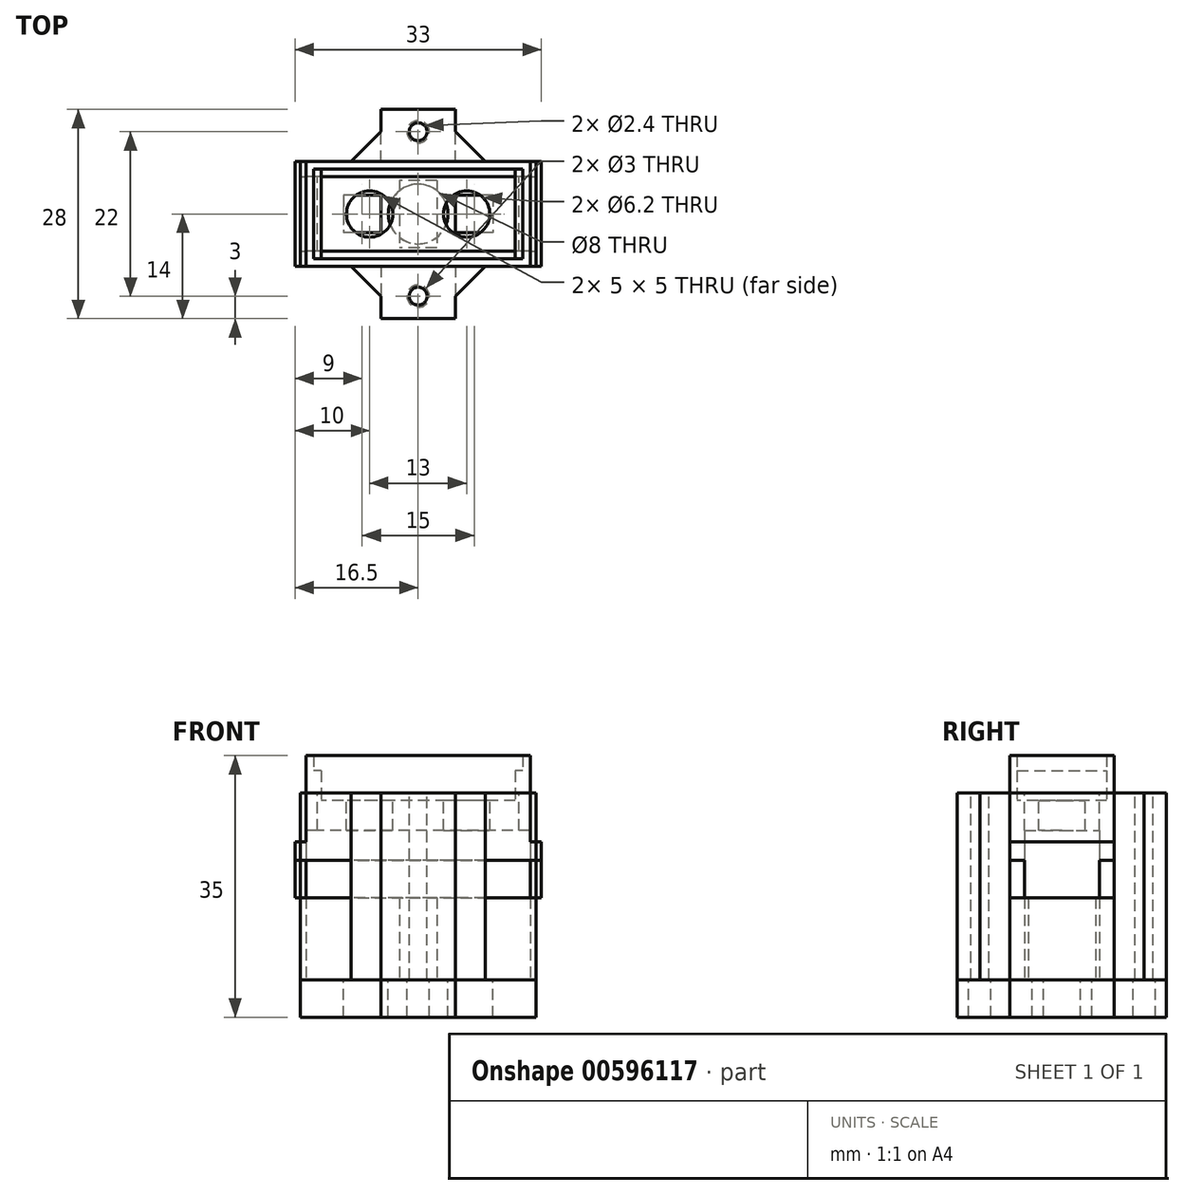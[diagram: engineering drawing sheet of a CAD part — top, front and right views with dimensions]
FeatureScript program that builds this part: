
annotation { "Feature Type Name" : "Feature", "Feature Type Description" : "" }
export const myFeature = defineFeature(function(context is Context, id is Id, definition is map)
    precondition{}
    {
        {
            var Q0;
            Q0=qCreatedBy(makeId("Top.planeOp"),FACE);
            var sketch = newSketch(context, id + "F0", { "sketchPlane" : qUnion([Q0])});
            skLineSegment(sketch, "E0.bottom", {"start": v(15, -7) * mm, "end": v(-15, -7) * mm});
            skLineSegment(sketch, "E0.top", {"start": v(15, 7) * mm, "end": v(-15, 7) * mm});
            skLineSegment(sketch, "E0.left", {"start": v(15, -7) * mm, "end": v(15, 7) * mm});
            skLineSegment(sketch, "E0.right", {"start": v(-15, -7) * mm, "end": v(-15, 7) * mm});
            skPoint(sketch, "E0.middle", {"position": v(0, 0) * mm});
            skSolve(sketch);
        }
        {
            var Q0;
            Q0=qSketchRegion(id+"F0",true);
            extrude(context, id + "F1", {"entities" : qUnion([Q0]), "depth" : 13 * mm, "offsetDistance" : 25 * mm});
        }
        {
            var Q0;
            Q0=makeQuery(id+"F1.opExtrude","CAP_FACE",FACE,{"disambiguationData":[OSD([sQuery(id+"F0.wireOp",EDGE,"E0.bottom"),sQuery(id+"F0.wireOp",EDGE,"E0.top"),sQuery(id+"F0.wireOp",EDGE,"E0.left"),sQuery(id+"F0.wireOp",EDGE,"E0.right")])],"isStart":false});
            var sketch = newSketch(context, id + "F2", { "sketchPlane" : qUnion([Q0])});
            skLineSegment(sketch, "E1.bottom", {"start": v(15, -7) * mm, "end": v(-15, -7) * mm});
            skLineSegment(sketch, "E1.top", {"start": v(15, 7) * mm, "end": v(-15, 7) * mm});
            skLineSegment(sketch, "E1.left", {"start": v(15, -7) * mm, "end": v(15, 7) * mm});
            skLineSegment(sketch, "E1.right", {"start": v(-15, -7) * mm, "end": v(-15, 7) * mm});
            skPoint(sketch, "E1.middle", {"position": v(0, 0) * mm});
            skLineSegment(sketch, "E2.bottom", {"start": v(14, -6) * mm, "end": v(-14, -6) * mm});
            skLineSegment(sketch, "E2.top", {"start": v(14, 6) * mm, "end": v(-14, 6) * mm});
            skLineSegment(sketch, "E2.left", {"start": v(14, -6) * mm, "end": v(14, 6) * mm});
            skLineSegment(sketch, "E2.right", {"start": v(-14, -6) * mm, "end": v(-14, 6) * mm});
            skSolve(sketch);
        }
        {
            var Q0;
            Q0=qSketchRegion(id+"F2",true);
            extrude(context, id + "F3", {"entities" : qUnion([Q0]), "operationType" : NewBodyOperationType.ADD, "depth" : 6 * mm, "offsetDistance" : 25 * mm});
        }
        {
            var Q0;
            Q0=makeQuery(id+"F1.opExtrude","CAP_FACE",FACE,{"disambiguationData":[OSD([sQuery(id+"F0.wireOp",EDGE,"E0.bottom"),sQuery(id+"F0.wireOp",EDGE,"E0.top"),sQuery(id+"F0.wireOp",EDGE,"E0.left"),sQuery(id+"F0.wireOp",EDGE,"E0.right")])],"isStart":false});
            var sketch = newSketch(context, id + "F4", { "sketchPlane" : qUnion([Q0])});
            skLineSegment(sketch, "E3.bottom", {"start": v(-14, 6) * mm, "end": v(-13, 6) * mm});
            skLineSegment(sketch, "E3.top", {"start": v(-14, -6) * mm, "end": v(-13, -6) * mm});
            skLineSegment(sketch, "E3.left", {"start": v(-14, 6) * mm, "end": v(-14, -6) * mm});
            skLineSegment(sketch, "E3.right", {"start": v(-13, 6) * mm, "end": v(-13, -6) * mm});
            skLineSegment(sketch, "E4.bottom", {"start": v(14, 6) * mm, "end": v(13, 6) * mm});
            skLineSegment(sketch, "E4.top", {"start": v(14, -6) * mm, "end": v(13, -6) * mm});
            skLineSegment(sketch, "E4.left", {"start": v(14, 6) * mm, "end": v(14, -6) * mm});
            skLineSegment(sketch, "E4.right", {"start": v(13, 6) * mm, "end": v(13, -6) * mm});
            skSolve(sketch);
        }
        {
            var Q0;
            Q0=qSketchRegion(id+"F4",true);
            extrude(context, id + "F5", {"entities" : qUnion([Q0]), "operationType" : NewBodyOperationType.ADD, "depth" : 4 * mm, "offsetDistance" : 25 * mm});
        }
        {
            var Q0;
            Q0=makeQuery(id+"F1.opExtrude","CAP_FACE",FACE,{"disambiguationData":[OSD([sQuery(id+"F0.wireOp",EDGE,"E0.bottom"),sQuery(id+"F0.wireOp",EDGE,"E0.top"),sQuery(id+"F0.wireOp",EDGE,"E0.left"),sQuery(id+"F0.wireOp",EDGE,"E0.right")])],"isStart":false});
            var sketch = newSketch(context, id + "F6", { "sketchPlane" : qUnion([Q0])});
            skCircle(sketch, "E5", {"center": v(-6.5, 0) * mm, "radius": 3.1 * mm});
            skCircle(sketch, "E6", {"center": v(6.5, 0) * mm, "radius": 3.1 * mm});
            skSolve(sketch);
        }
        {
            var Q0;
            Q0=qSketchRegion(id+"F6",true);
            extrude(context, id + "F7", {"entities" : qUnion([Q0]), "operationType" : NewBodyOperationType.REMOVE, "oppositeDirection" : true, "depth" : 19 * mm, "offsetDistance" : 25 * mm});
        }
        {
            var Q0;
            Q0=makeQuery(id+"F1.opExtrude","CAP_FACE",FACE,{"disambiguationData":[OSD([sQuery(id+"F0.wireOp",EDGE,"E0.bottom"),sQuery(id+"F0.wireOp",EDGE,"E0.top"),sQuery(id+"F0.wireOp",EDGE,"E0.left"),sQuery(id+"F0.wireOp",EDGE,"E0.right")])],"isStart":true});
            var sketch = newSketch(context, id + "F8", { "sketchPlane" : qUnion([Q0])});
            skLineSegment(sketch, "E7.bottom", {"start": v(-15, -7) * mm, "end": v(-16.5, -7) * mm});
            skLineSegment(sketch, "E7.top", {"start": v(-15, 7) * mm, "end": v(-16.5, 7) * mm});
            skLineSegment(sketch, "E7.left", {"start": v(-15, -7) * mm, "end": v(-15, 7) * mm});
            skLineSegment(sketch, "E7.right", {"start": v(-16.5, -7) * mm, "end": v(-16.5, 7) * mm});
            skLineSegment(sketch, "E8.bottom", {"start": v(15, -7) * mm, "end": v(16.5, -7) * mm});
            skLineSegment(sketch, "E8.top", {"start": v(15, 7) * mm, "end": v(16.5, 7) * mm});
            skLineSegment(sketch, "E8.left", {"start": v(15, -7) * mm, "end": v(15, 7) * mm});
            skLineSegment(sketch, "E8.right", {"start": v(16.5, -7) * mm, "end": v(16.5, 7) * mm});
            skSolve(sketch);
        }
        {
            var Q0;
            Q0=qSketchRegion(id+"F8",true);
            extrude(context, id + "F9", {"entities" : qUnion([Q0]), "operationType" : NewBodyOperationType.ADD, "oppositeDirection" : true, "depth" : 7.5 * mm, "offsetDistance" : 25 * mm});
        }
        {
            var Q0;
            Q0=makeQuery(id+"F9.boolean.opBoolean","MERGE",FACE,{"derivedFrom":[makeQuery(id+"F1.opExtrude","CAP_FACE",FACE,{"disambiguationData":[OSD([sQuery(id+"F0.wireOp",EDGE,"E0.bottom"),sQuery(id+"F0.wireOp",EDGE,"E0.top"),sQuery(id+"F0.wireOp",EDGE,"E0.left"),sQuery(id+"F0.wireOp",EDGE,"E0.right")])],"isStart":true}),makeQuery(id+"F9.opExtrude","CAP_FACE",FACE,{"disambiguationData":[OSD([sQuery(id+"F8.wireOp",EDGE,"E7.bottom"),sQuery(id+"F8.wireOp",EDGE,"E7.top"),sQuery(id+"F8.wireOp",EDGE,"E7.left"),sQuery(id+"F8.wireOp",EDGE,"E7.right")])],"isStart":true}),makeQuery(id+"F9.opExtrude","CAP_FACE",FACE,{"disambiguationData":[OSD([sQuery(id+"F8.wireOp",EDGE,"E8.bottom"),sQuery(id+"F8.wireOp",EDGE,"E8.top"),sQuery(id+"F8.wireOp",EDGE,"E8.left"),sQuery(id+"F8.wireOp",EDGE,"E8.right")])],"isStart":true})]});
            var sketch = newSketch(context, id + "F10", { "sketchPlane" : qUnion([Q0])});
            skCircle(sketch, "E9", {"center": v(0, 0) * mm, "radius": 2.55 * mm});
            skSolve(sketch);
        }
        {
            var Q0;
            Q0=qSketchRegion(id+"F10",true);
            extrude(context, id + "F11", {"entities" : qUnion([Q0]), "operationType" : NewBodyOperationType.REMOVE, "oppositeDirection" : true, "depth" : 3 * mm, "offsetDistance" : 25 * mm});
        }
        {
            var Q0;
            Q0=qCreatedBy(makeId("Top.planeOp"),FACE);
            cPlane(context, id + "F12", {"entities" : qUnion([Q0]), "cplaneType" : CPlaneType.OFFSET, "offset" : 14 * mm, "width" : 150 * mm, "height" : 150 * mm});
        }
        {
            var Q0;
            Q0=qCreatedBy(id+"F12.planeOp",FACE);
            var sketch = newSketch(context, id + "F13", { "sketchPlane" : qUnion([Q0])});
            skLineSegment(sketch, "E10.bottom", {"start": v(15.75, -7) * mm, "end": v(-15.75, -7) * mm});
            skLineSegment(sketch, "E10.top", {"start": v(15.75, 7) * mm, "end": v(-15.75, 7) * mm});
            skLineSegment(sketch, "E10.left", {"start": v(15.75, -7) * mm, "end": v(15.75, 7) * mm});
            skLineSegment(sketch, "E10.right", {"start": v(-15.75, -7) * mm, "end": v(-15.75, 7) * mm});
            skPoint(sketch, "E10.middle", {"position": v(0, 0) * mm});
            skLineSegment(sketch, "E11.bottom", {"start": v(-5, 7) * mm, "end": v(5, 7) * mm});
            skLineSegment(sketch, "E11.top", {"start": v(-5, 14) * mm, "end": v(5, 14) * mm});
            skLineSegment(sketch, "E11.left", {"start": v(-5, 7) * mm, "end": v(-5, 14) * mm});
            skLineSegment(sketch, "E11.right", {"start": v(5, 7) * mm, "end": v(5, 14) * mm});
            skLineSegment(sketch, "E12.bottom", {"start": v(-5, -7) * mm, "end": v(5, -7) * mm});
            skLineSegment(sketch, "E12.top", {"start": v(-5, -14) * mm, "end": v(5, -14) * mm});
            skLineSegment(sketch, "E12.left", {"start": v(-5, -7) * mm, "end": v(-5, -14) * mm});
            skLineSegment(sketch, "E12.right", {"start": v(5, -7) * mm, "end": v(5, -14) * mm});
            skLineSegment(sketch, "E13.bottom", {"start": v(13.5, -5) * mm, "end": v(-13.5, -5) * mm});
            skLineSegment(sketch, "E13.top", {"start": v(13.5, 5) * mm, "end": v(-13.5, 5) * mm});
            skLineSegment(sketch, "E13.left", {"start": v(13.5, -5) * mm, "end": v(13.5, 5) * mm});
            skLineSegment(sketch, "E13.right", {"start": v(-13.5, -5) * mm, "end": v(-13.5, 5) * mm});
            skSolve(sketch);
        }
        {
            var Q0;
            Q0=qSketchRegion(id+"F13",true);
            extrude(context, id + "F14", {"entities" : qUnion([Q0]), "oppositeDirection" : true, "depth" : 25 * mm, "offsetDistance" : 25 * mm});
        }
        {
            var Q0;
            Q0=makeQuery(id+"F14.opExtrude","CAP_FACE",FACE,{"disambiguationData":[OSD([sQuery(id+"F13.wireOp",EDGE,"E10.bottom"),sQuery(id+"F13.wireOp",EDGE,"E10.top"),sQuery(id+"F13.wireOp",EDGE,"E10.left"),sQuery(id+"F13.wireOp",EDGE,"E10.right"),sQuery(id+"F13.wireOp",EDGE,"E11.top"),sQuery(id+"F13.wireOp",EDGE,"E11.left"),sQuery(id+"F13.wireOp",EDGE,"E11.right"),sQuery(id+"F13.wireOp",EDGE,"E12.top"),sQuery(id+"F13.wireOp",EDGE,"E12.left"),sQuery(id+"F13.wireOp",EDGE,"E12.right")])],"isStart":false});
            var sketch = newSketch(context, id + "F15", { "sketchPlane" : qUnion([Q0])});
            skLineSegment(sketch, "E14.bottom", {"start": v(15, -5) * mm, "end": v(-15, -5) * mm});
            skLineSegment(sketch, "E14.top", {"start": v(15, 5) * mm, "end": v(-15, 5) * mm});
            skLineSegment(sketch, "E14.left", {"start": v(15, -5) * mm, "end": v(15, 5) * mm});
            skLineSegment(sketch, "E14.right", {"start": v(-15, -5) * mm, "end": v(-15, 5) * mm});
            skPoint(sketch, "E14.middle", {"position": v(0, 0) * mm});
            skSolve(sketch);
        }
        {
            var Q0;
            Q0=qSketchRegion(id+"F15",true);
            extrude(context, id + "F16", {"entities" : qUnion([Q0]), "operationType" : NewBodyOperationType.REMOVE, "oppositeDirection" : true, "depth" : 20 * mm, "offsetDistance" : 25 * mm});
        }
        {
            var Q0;
            Q0=makeQuery(id+"F14.opExtrude","CAP_FACE",FACE,{"disambiguationData":[OSD([sQuery(id+"F13.wireOp",EDGE,"E10.bottom"),sQuery(id+"F13.wireOp",EDGE,"E10.top"),sQuery(id+"F13.wireOp",EDGE,"E10.left"),sQuery(id+"F13.wireOp",EDGE,"E10.right"),sQuery(id+"F13.wireOp",EDGE,"E11.top"),sQuery(id+"F13.wireOp",EDGE,"E11.left"),sQuery(id+"F13.wireOp",EDGE,"E11.right"),sQuery(id+"F13.wireOp",EDGE,"E12.top"),sQuery(id+"F13.wireOp",EDGE,"E12.left"),sQuery(id+"F13.wireOp",EDGE,"E12.right")])],"isStart":true});
            var sketch = newSketch(context, id + "F17", { "sketchPlane" : qUnion([Q0])});
            skCircle(sketch, "E15", {"center": v(0, 11) * mm, "radius": 1.2 * mm});
            skCircle(sketch, "E16", {"center": v(0, -11) * mm, "radius": 1.2 * mm});
            skSolve(sketch);
        }
        {
            var Q0;
            Q0=qSketchRegion(id+"F17",true);
            extrude(context, id + "F18", {"entities" : qUnion([Q0]), "operationType" : NewBodyOperationType.REMOVE, "oppositeDirection" : true, "depth" : 25 * mm, "offsetDistance" : 25 * mm});
        }
        {
            var Q0;
            Q0=makeQuery(id+"F14.opExtrude","CAP_FACE",FACE,{"disambiguationData":[OSD([sQuery(id+"F13.wireOp",EDGE,"E10.bottom"),sQuery(id+"F13.wireOp",EDGE,"E10.top"),sQuery(id+"F13.wireOp",EDGE,"E10.left"),sQuery(id+"F13.wireOp",EDGE,"E10.right"),sQuery(id+"F13.wireOp",EDGE,"E11.top"),sQuery(id+"F13.wireOp",EDGE,"E11.left"),sQuery(id+"F13.wireOp",EDGE,"E11.right"),sQuery(id+"F13.wireOp",EDGE,"E12.top"),sQuery(id+"F13.wireOp",EDGE,"E12.left"),sQuery(id+"F13.wireOp",EDGE,"E12.right"),sQuery(id+"F13.wireOp",EDGE,"E13.bottom"),sQuery(id+"F13.wireOp",EDGE,"E13.top"),sQuery(id+"F13.wireOp",EDGE,"E13.left"),sQuery(id+"F13.wireOp",EDGE,"E13.right")])],"isStart":false});
            var sketch = newSketch(context, id + "F19", { "sketchPlane" : qUnion([Q0])});
            skLineSegment(sketch, "E17.bottom", {"start": v(15.75, -7) * mm, "end": v(-15.75, -7) * mm});
            skLineSegment(sketch, "E17.top", {"start": v(15.75, 7) * mm, "end": v(-15.75, 7) * mm});
            skLineSegment(sketch, "E17.left", {"start": v(15.75, -7) * mm, "end": v(15.75, 7) * mm});
            skLineSegment(sketch, "E17.right", {"start": v(-15.75, -7) * mm, "end": v(-15.75, 7) * mm});
            skPoint(sketch, "E17.middle", {"position": v(0, 0) * mm});
            skLineSegment(sketch, "E18.bottom", {"start": v(-5, 7) * mm, "end": v(5, 7) * mm});
            skLineSegment(sketch, "E18.top", {"start": v(-5, 14) * mm, "end": v(5, 14) * mm});
            skLineSegment(sketch, "E18.left", {"start": v(-5, 7) * mm, "end": v(-5, 14) * mm});
            skLineSegment(sketch, "E18.right", {"start": v(5, 7) * mm, "end": v(5, 14) * mm});
            skLineSegment(sketch, "E19.bottom", {"start": v(5, -7) * mm, "end": v(-5, -7) * mm});
            skLineSegment(sketch, "E19.top", {"start": v(5, -14) * mm, "end": v(-5, -14) * mm});
            skLineSegment(sketch, "E19.left", {"start": v(5, -7) * mm, "end": v(5, -14) * mm});
            skLineSegment(sketch, "E19.right", {"start": v(-5, -7) * mm, "end": v(-5, -14) * mm});
            skCircle(sketch, "E20", {"center": v(0, 0) * mm, "radius": 4 * mm});
            skLineSegment(sketch, "E21.bottom", {"start": v(-5, -2.5) * mm, "end": v(-10, -2.5) * mm});
            skLineSegment(sketch, "E21.top", {"start": v(-5, 2.5) * mm, "end": v(-10, 2.5) * mm});
            skLineSegment(sketch, "E21.left", {"start": v(-5, -2.5) * mm, "end": v(-5, 2.5) * mm});
            skLineSegment(sketch, "E21.right", {"start": v(-10, -2.5) * mm, "end": v(-10, 2.5) * mm});
            skPoint(sketch, "E21.middle", {"position": v(-7.5, 0) * mm});
            skLineSegment(sketch, "E22.bottom", {"start": v(10, -2.5) * mm, "end": v(5, -2.5) * mm});
            skLineSegment(sketch, "E22.top", {"start": v(10, 2.5) * mm, "end": v(5, 2.5) * mm});
            skLineSegment(sketch, "E22.left", {"start": v(10, -2.5) * mm, "end": v(10, 2.5) * mm});
            skLineSegment(sketch, "E22.right", {"start": v(5, -2.5) * mm, "end": v(5, 2.5) * mm});
            skPoint(sketch, "E22.middle", {"position": v(7.5, 0) * mm});
            skCircle(sketch, "E23", {"center": v(0, 11) * mm, "radius": 1.5 * mm});
            skCircle(sketch, "E24", {"center": v(0, -11) * mm, "radius": 1.5 * mm});
            skSolve(sketch);
        }
        {
            var Q0;
            Q0=qSketchRegion(id+"F19",true);
            extrude(context, id + "F20", {"entities" : qUnion([Q0]), "depth" : 5 * mm, "offsetDistance" : 25 * mm});
        }
        {
            var Q0;
            Q0=makeQuery(id+"F14.opExtrude","SWEPT_EDGE",EDGE,{"disambiguationData":[OSD([sQuery(id+"F13.wireOp",EDGE,"E10.top"),sQuery(id+"F13.wireOp",EDGE,"E11.bottom"),sQuery(id+"F13.wireOp",EDGE,"E11.left")])]});
            var Q1;
            Q1=makeQuery(id+"F14.opExtrude","SWEPT_EDGE",EDGE,{"disambiguationData":[OSD([sQuery(id+"F13.wireOp",EDGE,"E10.top"),sQuery(id+"F13.wireOp",EDGE,"E11.bottom"),sQuery(id+"F13.wireOp",EDGE,"E11.right")])]});
            var Q2;
            Q2=makeQuery(id+"F14.opExtrude","SWEPT_EDGE",EDGE,{"disambiguationData":[OSD([sQuery(id+"F13.wireOp",EDGE,"E10.bottom"),sQuery(id+"F13.wireOp",EDGE,"E12.bottom"),sQuery(id+"F13.wireOp",EDGE,"E12.right")])]});
            var Q3;
            Q3=makeQuery(id+"F14.opExtrude","SWEPT_EDGE",EDGE,{"disambiguationData":[OSD([sQuery(id+"F13.wireOp",EDGE,"E10.bottom"),sQuery(id+"F13.wireOp",EDGE,"E12.bottom"),sQuery(id+"F13.wireOp",EDGE,"E12.left")])]});
            chamfer(context, id + "F21", {"entities" : qUnion([Q0, Q1, Q2, Q3]), "width" : 4 * mm, "tangentPropagation" : true});
        }
        {
            var Q0;
            Q0=makeQuery(id+"F14.opExtrude","CAP_FACE",FACE,{"disambiguationData":[OSD([sQuery(id+"F13.wireOp",EDGE,"E10.bottom"),sQuery(id+"F13.wireOp",EDGE,"E10.top"),sQuery(id+"F13.wireOp",EDGE,"E10.left"),sQuery(id+"F13.wireOp",EDGE,"E10.right"),sQuery(id+"F13.wireOp",EDGE,"E11.top"),sQuery(id+"F13.wireOp",EDGE,"E11.left"),sQuery(id+"F13.wireOp",EDGE,"E11.right"),sQuery(id+"F13.wireOp",EDGE,"E12.top"),sQuery(id+"F13.wireOp",EDGE,"E12.left"),sQuery(id+"F13.wireOp",EDGE,"E12.right"),sQuery(id+"F13.wireOp",EDGE,"E13.bottom"),sQuery(id+"F13.wireOp",EDGE,"E13.top"),sQuery(id+"F13.wireOp",EDGE,"E13.left"),sQuery(id+"F13.wireOp",EDGE,"E13.right")])],"isStart":false});
            cPlane(context, id + "F22", {"entities" : qUnion([Q0]), "cplaneType" : CPlaneType.OFFSET, "offset" : 0 * mm, "width" : 150 * mm, "height" : 150 * mm});
        }
        {
            var Q0;
            Q0=qCreatedBy(id+"F22.planeOp",FACE);
            var sketch = newSketch(context, id + "F23", { "sketchPlane" : qUnion([Q0])});
            skLineSegment(sketch, "E25.bottom", {"start": v(2.5, -4.5) * mm, "end": v(-2.5, -4.5) * mm});
            skLineSegment(sketch, "E25.top", {"start": v(2.5, 4.5) * mm, "end": v(-2.5, 4.5) * mm});
            skLineSegment(sketch, "E25.left", {"start": v(2.5, -4.5) * mm, "end": v(2.5, 4.5) * mm});
            skLineSegment(sketch, "E25.right", {"start": v(-2.5, -4.5) * mm, "end": v(-2.5, 4.5) * mm});
            skPoint(sketch, "E25.middle", {"position": v(0, 0) * mm});
            skLineSegment(sketch, "E26.0", {"start": v(15, 5) * mm, "end": v(-15, 5) * mm});
            skLineSegment(sketch, "E26.1", {"start": v(15, -5) * mm, "end": v(-15, -5) * mm});
            skPoint(sketch, "E27", {"position": v(0, 5) * mm});
            skSolve(sketch);
        }
        {
            var Q0;
            Q0=qSketchRegion(id+"F23",true);
            extrude(context, id + "F24", {"entities" : qUnion([Q0]), "oppositeDirection" : true, "depth" : 11 * mm, "offsetDistance" : 25 * mm});
        }
        {
            var Q0;
            Q0=makeQuery(id+"F9.boolean.opBoolean","MERGE",FACE,{"derivedFrom":[makeQuery(id+"F1.opExtrude","CAP_FACE",FACE,{"disambiguationData":[OSD([sQuery(id+"F0.wireOp",EDGE,"E0.bottom"),sQuery(id+"F0.wireOp",EDGE,"E0.top"),sQuery(id+"F0.wireOp",EDGE,"E0.left"),sQuery(id+"F0.wireOp",EDGE,"E0.right")])],"isStart":true}),makeQuery(id+"F9.opExtrude","CAP_FACE",FACE,{"disambiguationData":[OSD([sQuery(id+"F8.wireOp",EDGE,"E7.bottom"),sQuery(id+"F8.wireOp",EDGE,"E7.top"),sQuery(id+"F8.wireOp",EDGE,"E7.left"),sQuery(id+"F8.wireOp",EDGE,"E7.right")])],"isStart":true}),makeQuery(id+"F9.opExtrude","CAP_FACE",FACE,{"disambiguationData":[OSD([sQuery(id+"F8.wireOp",EDGE,"E8.bottom"),sQuery(id+"F8.wireOp",EDGE,"E8.top"),sQuery(id+"F8.wireOp",EDGE,"E8.left"),sQuery(id+"F8.wireOp",EDGE,"E8.right")])],"isStart":true})]});
            var sketch = newSketch(context, id + "F25", { "sketchPlane" : qUnion([Q0])});
            skLineSegment(sketch, "E28.bottom", {"start": v(-16.5, 7) * mm, "end": v(16.5, 7) * mm});
            skLineSegment(sketch, "E28.top", {"start": v(-16.5, 5) * mm, "end": v(16.5, 5) * mm});
            skLineSegment(sketch, "E28.left", {"start": v(-16.5, 7) * mm, "end": v(-16.5, 5) * mm});
            skLineSegment(sketch, "E28.right", {"start": v(16.5, 7) * mm, "end": v(16.5, 5) * mm});
            skLineSegment(sketch, "E29.bottom", {"start": v(16.5, -7) * mm, "end": v(-16.5, -7) * mm});
            skLineSegment(sketch, "E29.top", {"start": v(16.5, -5) * mm, "end": v(-16.5, -5) * mm});
            skLineSegment(sketch, "E29.left", {"start": v(16.5, -7) * mm, "end": v(16.5, -5) * mm});
            skLineSegment(sketch, "E29.right", {"start": v(-16.5, -7) * mm, "end": v(-16.5, -5) * mm});
            skSolve(sketch);
        }
        {
            var Q0;
            Q0 = qSketchRegion(id + "F25", true);
            extrude(context, id + "F26", {"entities" : qUnion([Q0]), "operationType" : NewBodyOperationType.REMOVE, "oppositeDirection" : true, "depth" : 5 * mm, "offsetDistance" : 25 * mm});
        }
    });
